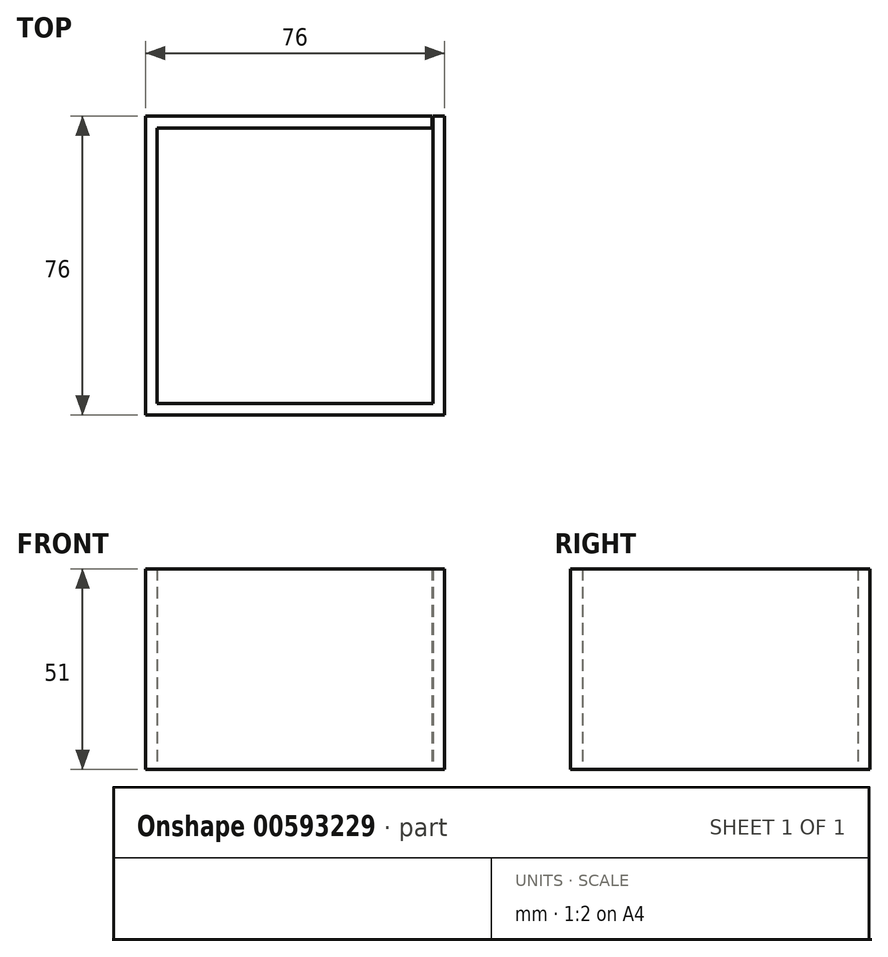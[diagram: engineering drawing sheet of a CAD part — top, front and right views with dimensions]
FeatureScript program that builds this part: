
annotation { "Feature Type Name" : "Feature", "Feature Type Description" : "" }
export const myFeature = defineFeature(function(context is Context, id is Id, definition is map)
    precondition{}
    {
        {
            var Q0;
            Q0=qCreatedBy(makeId("Top.planeOp"),FACE);
            var sketch = newSketch(context, id + "F0", { "sketchPlane" : qUnion([Q0])});
            skLineSegment(sketch, "E0.bottom", {"start": v(0, 70) * mm, "end": v(69.8, 70) * mm});
            skLineSegment(sketch, "E0.top", {"start": v(0, 0) * mm, "end": v(70, 0) * mm});
            skLineSegment(sketch, "E0.left", {"start": v(0, 70) * mm, "end": v(0, 0) * mm});
            skLineSegment(sketch, "E0.right", {"start": v(70, 70) * mm, "end": v(70, 0) * mm});
            skLineSegment(sketch, "E1.bottom", {"start": v(-3, 73) * mm, "end": v(69.8, 73) * mm});
            skLineSegment(sketch, "E1.top", {"start": v(-3, -3) * mm, "end": v(73, -3) * mm});
            skLineSegment(sketch, "E1.left", {"start": v(-3, 73) * mm, "end": v(-3, -3) * mm});
            skLineSegment(sketch, "E1.right", {"start": v(73, 73) * mm, "end": v(73, -3) * mm});
            skLineSegment(sketch, "E2", {"start": v(70, 70) * mm, "end": v(70, 73) * mm});
            skLineSegment(sketch, "E3", {"start": v(69.8, 73) * mm, "end": v(69.8, 70) * mm});
            skLineSegment(sketch, "E4.trimOffspring", {"start": v(70, 73) * mm, "end": v(73, 73) * mm});
            skSolve(sketch);
        }
        {
            var Q0;
            Q0=qSketchRegion(id+"F0",true);
            extrude(context, id + "F1", {"entities" : qUnion([Q0]), "depth" : 54 * mm, "offsetDistance" : 25 * mm, "hasSecondDirection" : true, "secondDirectionOppositeDirection" : true, "secondDirectionDepth" : -3 * mm});
        }
    });
